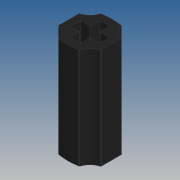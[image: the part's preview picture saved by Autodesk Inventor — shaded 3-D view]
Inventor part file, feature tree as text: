
AUTODESK INVENTOR PART (.ipt)
format: ipt  version: 2022.2 (Build 262287000, 287)  size: 165,888 bytes
history: native  units: in
note: dims shown in document units (in); Inventor stores cm internally (conversion verified against a paired STEP export)
features: extrude x2, sketch x1, fillet x1
ambient origin geometry x8: Origin, YZ Plane, XZ Plane, XY Plane, X Axis, Y Axis, Z Axis, Center Point
bodies: Solid1 (feature_tree)
feature tree (4):
  sketch  "Sketch2"  dims[d0=0.1873in d1=0.2772in d2=0.315in d4=0.063in d5=0.6299in d6=0.0in d19=0.0039in d20=0.189in d21=0.7441in d22=0.2677in d23=0.0079in d24=0.0in d25=0.0in]
  extrude  "Extrusion1"  Depth=0.0079in
  extrude  "Extrusion3"  Depth=0.315in
  fillet  "Fillet1"  Radius=0.063in
